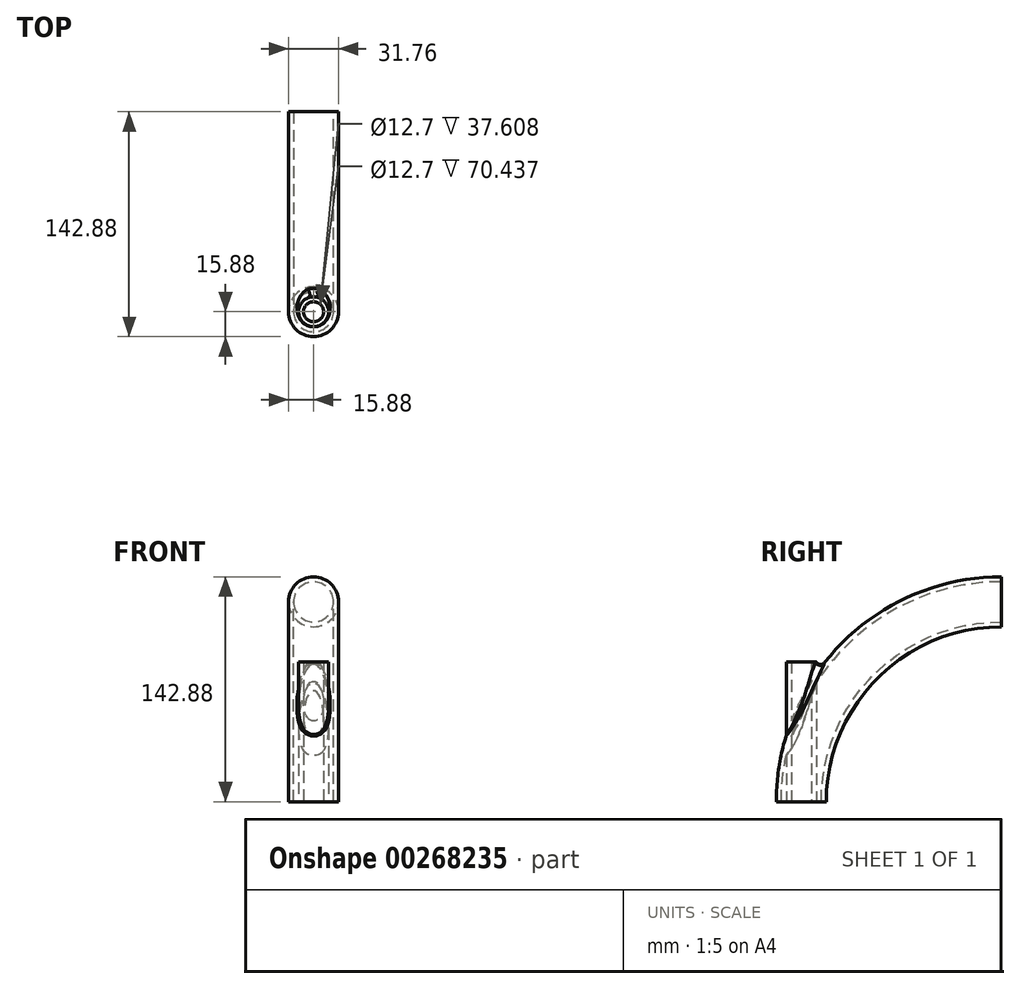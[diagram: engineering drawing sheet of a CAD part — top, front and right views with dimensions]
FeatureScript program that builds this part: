
annotation { "Feature Type Name" : "Feature", "Feature Type Description" : "" }
export const myFeature = defineFeature(function(context is Context, id is Id, definition is map)
    precondition{}
    {
        {
            var Q0;
            Q0=qCreatedBy(makeId("Right.planeOp"),FACE);
            var sketch = newSketch(context, id + "F0", { "sketchPlane" : qUnion([Q0])});
            skArc(sketch, "E0", {"start": v(0, 0) * mm, "mid": v(37.2, 89.8) * mm, "end": v(127, 127) * mm});
            skLineSegment(sketch, "E1", {"start": v(0, 0) * mm, "end": v(127, 0) * mm, "construction": true});
            skLineSegment(sketch, "E2", {"start": v(127, 127) * mm, "end": v(127, 0) * mm, "construction": true});
            skSolve(sketch);
        }
        {
            var Q0;
            Q0=qCreatedBy(makeId("Top.planeOp"),FACE);
            var sketch = newSketch(context, id + "F1", { "sketchPlane" : qUnion([Q0])});
            skCircle(sketch, "E3", {"center": v(0, 0) * mm, "radius": 12.7 * mm});
            skCircle(sketch, "E4", {"center": v(0, 0) * mm, "radius": 15.88 * mm});
            skSolve(sketch);
        }
        {
            var Q0;
            Q0=makeQuery(id+"F1.imprint","IMPRINT",FACE,{"disambiguationData":[TD([[makeQuery(id+"F1.imprint","IMPRINT",EDGE,{"derivedFrom":sQuery(id+"F1.wireOp",EDGE,"E3")}),-1.0]])]});
            var Q1;
            Q1=sQuery(id+"F0.wireOp",EDGE,"E0");
            sweep(context, id + "F2", {"profiles" : qUnion([Q0]), "path" : qUnion([Q1])});
        }
        {
            var Q0;
            Q0=qCreatedBy(makeId("Top.planeOp"),FACE);
            var sketch = newSketch(context, id + "F3", { "sketchPlane" : qUnion([Q0])});
            skCircle(sketch, "E5", {"center": v(0, 0) * mm, "radius": 9.52 * mm});
            skCircle(sketch, "E6", {"center": v(0, 0) * mm, "radius": 6.35 * mm});
            skSolve(sketch);
        }
        {
            var Q0;
            Q0 = qSketchRegion(id + "F3", true);
            extrude(context, id + "F4", {"entities" : qUnion([Q0]), "operationType" : NewBodyOperationType.ADD, "depth" : 88.9 * mm});
        }
        {
            var Q0;
            Q0=makeQuery(id+"F4.boolean.opBoolean","INTERSECT",EDGE,{"derivedFrom":[makeQuery(id+"F2.opSweep","SWEPT_FACE",FACE,{"disambiguationData":[OSD([sQuery(id+"F0.wireOp",EDGE,"E0"),sQuery(id+"F1.wireOp",EDGE,"E4")])]}),makeQuery(id+"F4.opExtrude","SWEPT_FACE",FACE,{"disambiguationData":[OSD([sQuery(id+"F3.wireOp",EDGE,"E5")])]})]});
            fillet(context, id + "F5", {"entities" : qUnion([Q0]), "radius" : 3.17 * mm, "tangentPropagation" : true, "allowEdgeOverflow" : false});
        }
    });
